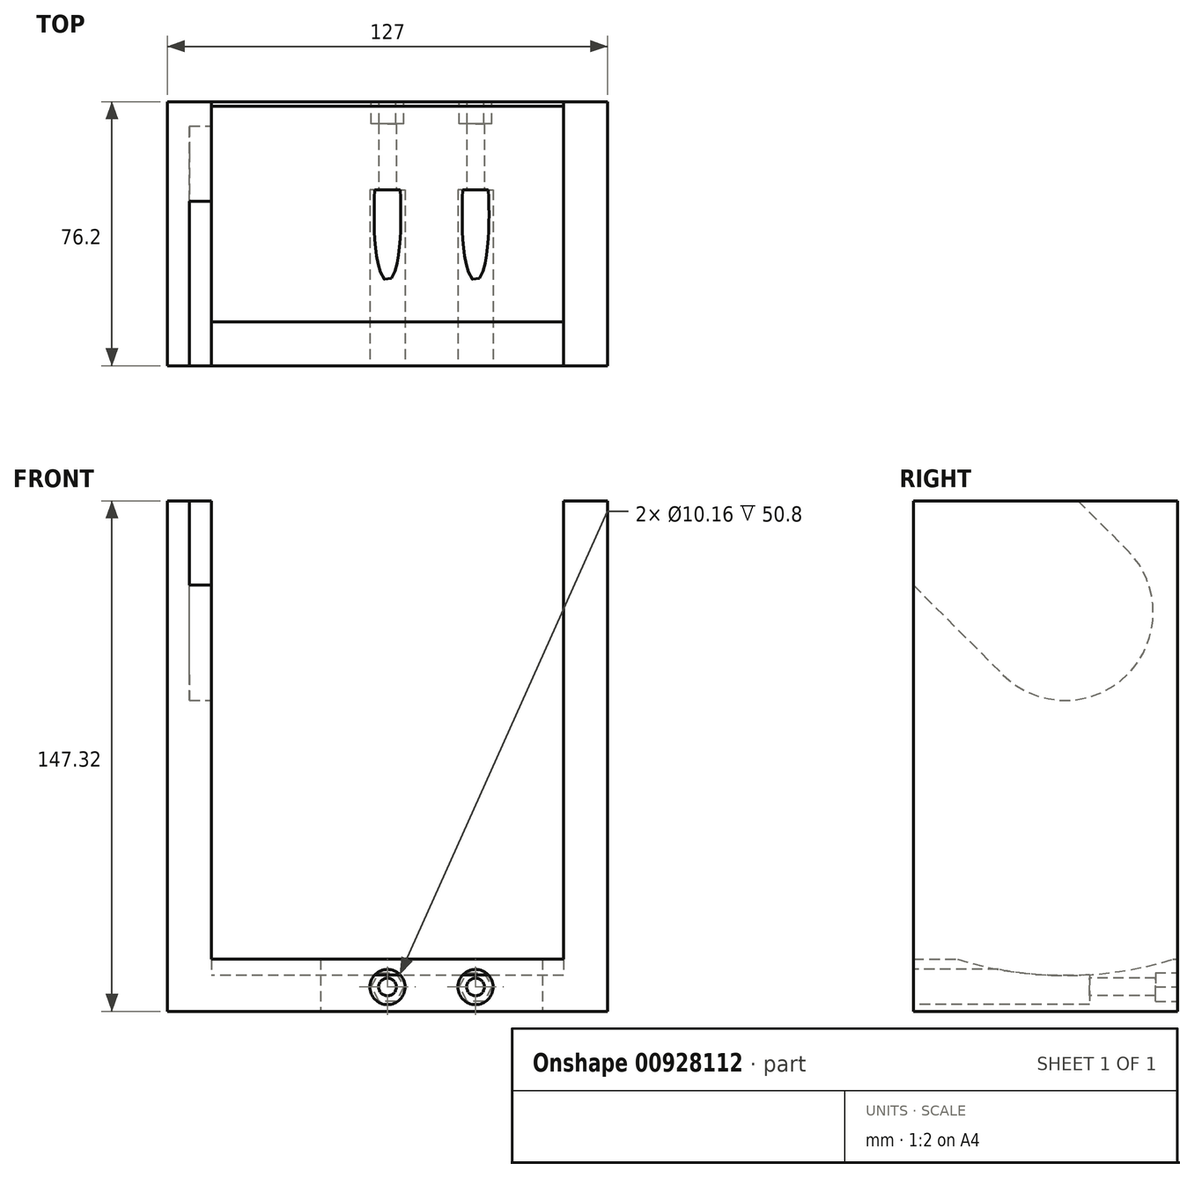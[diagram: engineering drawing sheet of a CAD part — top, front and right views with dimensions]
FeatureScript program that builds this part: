
annotation { "Feature Type Name" : "Feature", "Feature Type Description" : "" }
export const myFeature = defineFeature(function(context is Context, id is Id, definition is map)
    precondition{}
    {
        {
            var Q0;
            Q0=qCreatedBy(makeId("Top.planeOp"),FACE);
            var sketch = newSketch(context, id + "F0", { "sketchPlane" : qUnion([Q0])});
            skLineSegment(sketch, "E0.bottom", {"start": v(38.1, -38.1) * mm, "end": v(-38.1, -38.1) * mm});
            skLineSegment(sketch, "E0.top", {"start": v(38.1, 38.1) * mm, "end": v(-38.1, 38.1) * mm});
            skLineSegment(sketch, "E0.left", {"start": v(38.1, -38.1) * mm, "end": v(38.1, 38.1) * mm});
            skPoint(sketch, "E0.middle", {"position": v(0, 0) * mm});
            skLineSegment(sketch, "E1.bottom", {"start": v(-38.1, -38.1) * mm, "end": v(-63.5, -38.1) * mm});
            skLineSegment(sketch, "E1.top", {"start": v(-38.1, 38.1) * mm, "end": v(-63.5, 38.1) * mm});
            skLineSegment(sketch, "E1.right", {"start": v(-63.5, -38.1) * mm, "end": v(-63.5, 38.1) * mm});
            skSolve(sketch);
        }
        {
            var Q0;
            Q0 = qSketchRegion(id + "F0", true);
            extrude(context, id + "F1", {"entities" : qUnion([Q0]), "depth" : 15 * mm, "offsetDistance" : 25.4 * mm});
        }
        {
            var Q0;
            Q0=qCreatedBy(makeId("Top.planeOp"),FACE);
            var sketch = newSketch(context, id + "F2", { "sketchPlane" : qUnion([Q0])});
            skLineSegment(sketch, "E2.bottom", {"start": v(-63.5, -38.1) * mm, "end": v(-76.2, -38.1) * mm});
            skLineSegment(sketch, "E2.top", {"start": v(-63.5, 38.1) * mm, "end": v(-76.2, 38.1) * mm});
            skLineSegment(sketch, "E2.left", {"start": v(-63.5, -38.1) * mm, "end": v(-63.5, 38.1) * mm});
            skLineSegment(sketch, "E2.right", {"start": v(-76.2, -38.1) * mm, "end": v(-76.2, 38.1) * mm});
            skLineSegment(sketch, "E3.bottom", {"start": v(38.1, -38.1) * mm, "end": v(50.8, -38.1) * mm});
            skLineSegment(sketch, "E3.top", {"start": v(38.1, 38.1) * mm, "end": v(50.8, 38.1) * mm});
            skLineSegment(sketch, "E3.left", {"start": v(38.1, -38.1) * mm, "end": v(38.1, 38.1) * mm});
            skLineSegment(sketch, "E3.right", {"start": v(50.8, -38.1) * mm, "end": v(50.8, 38.1) * mm});
            skSolve(sketch);
        }
        {
            var Q0;
            Q0 = qSketchRegion(id + "F2", true);
            extrude(context, id + "F3", {"entities" : qUnion([Q0]), "operationType" : NewBodyOperationType.ADD, "depth" : 147.32 * mm, "offsetDistance" : 25.4 * mm});
        }
        {
            var Q0;
            Q0=makeQuery(id+"F3.boolean.opBoolean","MERGE",FACE,{"derivedFrom":[makeQuery(id+"F1.opExtrude","SWEPT_FACE",FACE,{"disambiguationData":[OSD([sQuery(id+"F0.wireOp",EDGE,"E0.bottom")])]}),makeQuery(id+"F3.opExtrude","SWEPT_FACE",FACE,{"disambiguationData":[OSD([sQuery(id+"F2.wireOp",EDGE,"E2.bottom")])]}),makeQuery(id+"F3.opExtrude","SWEPT_FACE",FACE,{"disambiguationData":[OSD([sQuery(id+"F2.wireOp",EDGE,"E3.bottom")])]})]});
            var sketch = newSketch(context, id + "F4", { "sketchPlane" : qUnion([Q0])});
            skCircle(sketch, "E4", {"center": v(-12.7, 7.01) * mm, "radius": 2.54 * mm});
            skCircle(sketch, "E5", {"center": v(12.7, 7.01) * mm, "radius": 2.54 * mm});
            skLineSegment(sketch, "E6", {"start": v(-12.7, 7.01) * mm, "end": v(12.7, 7.01) * mm, "construction": true});
            skLineSegment(sketch, "E7", {"start": v(0, 7.01) * mm, "end": v(0, 11.5) * mm});
            skSolve(sketch);
        }
        {
            var Q0;
            Q0 = qSketchRegion(id + "F4", true);
            extrude(context, id + "F5", {"entities" : qUnion([Q0]), "operationType" : NewBodyOperationType.REMOVE, "endBound" : BoundingType.THROUGH_ALL, "oppositeDirection" : true, "depth" : 25.4 * mm, "offsetDistance" : 25.4 * mm});
        }
        {
            var Q0;
            Q0=makeQuery(id+"F3.boolean.opBoolean","MERGE",FACE,{"derivedFrom":[makeQuery(id+"F1.opExtrude","SWEPT_FACE",FACE,{"disambiguationData":[OSD([sQuery(id+"F0.wireOp",EDGE,"E0.top")])]}),makeQuery(id+"F3.opExtrude","SWEPT_FACE",FACE,{"disambiguationData":[OSD([sQuery(id+"F2.wireOp",EDGE,"E2.top")])]}),makeQuery(id+"F3.opExtrude","SWEPT_FACE",FACE,{"disambiguationData":[OSD([sQuery(id+"F2.wireOp",EDGE,"E3.top")])]})]});
            var sketch = newSketch(context, id + "F6", { "sketchPlane" : qUnion([Q0])});
            skCircle(sketch, "E8.cCircle", {"center": v(-12.7, 7.01) * mm, "radius": 4.11 * mm, "construction": true});
            skLineSegment(sketch, "E8.0", {"start": v(-10.33, 11.12) * mm, "end": v(-7.95, 7.01) * mm});
            skLineSegment(sketch, "E8.1", {"start": v(-7.95, 7.01) * mm, "end": v(-10.33, 2.9) * mm});
            skLineSegment(sketch, "E8.2", {"start": v(-10.33, 2.9) * mm, "end": v(-15.07, 2.9) * mm});
            skLineSegment(sketch, "E8.3", {"start": v(-15.07, 2.9) * mm, "end": v(-17.45, 7.01) * mm});
            skLineSegment(sketch, "E8.4", {"start": v(-17.45, 7.01) * mm, "end": v(-15.07, 11.12) * mm});
            skLineSegment(sketch, "E8.5", {"start": v(-15.07, 11.12) * mm, "end": v(-10.33, 11.12) * mm});
            skPoint(sketch, "E8.0.midPoint", {"position": v(-9.14, 9.07) * mm});
            skCircle(sketch, "E9.cCircle", {"center": v(12.7, 7.01) * mm, "radius": 4.11 * mm, "construction": true});
            skLineSegment(sketch, "E9.0", {"start": v(15.07, 11.12) * mm, "end": v(17.45, 7.01) * mm});
            skLineSegment(sketch, "E9.1", {"start": v(17.45, 7.01) * mm, "end": v(15.07, 2.9) * mm});
            skLineSegment(sketch, "E9.2", {"start": v(15.07, 2.9) * mm, "end": v(10.33, 2.9) * mm});
            skLineSegment(sketch, "E9.3", {"start": v(10.33, 2.9) * mm, "end": v(7.95, 7.01) * mm});
            skLineSegment(sketch, "E9.4", {"start": v(7.95, 7.01) * mm, "end": v(10.33, 11.12) * mm});
            skLineSegment(sketch, "E9.5", {"start": v(10.33, 11.12) * mm, "end": v(15.07, 11.12) * mm});
            skPoint(sketch, "E9.0.midPoint", {"position": v(16.26, 9.07) * mm});
            skSolve(sketch);
        }
        {
            var Q0;
            Q0 = qSketchRegion(id + "F6", true);
            extrude(context, id + "F7", {"entities" : qUnion([Q0]), "operationType" : NewBodyOperationType.REMOVE, "oppositeDirection" : true, "depth" : 6.35 * mm, "offsetDistance" : 25.4 * mm});
        }
        {
            var Q0;
            Q0=makeQuery(id+"F3.boolean.opBoolean","MERGE",FACE,{"derivedFrom":[makeQuery(id+"F1.opExtrude","SWEPT_FACE",FACE,{"disambiguationData":[OSD([sQuery(id+"F0.wireOp",EDGE,"E0.bottom")])]}),makeQuery(id+"F3.opExtrude","SWEPT_FACE",FACE,{"disambiguationData":[OSD([sQuery(id+"F2.wireOp",EDGE,"E2.bottom")])]}),makeQuery(id+"F3.opExtrude","SWEPT_FACE",FACE,{"disambiguationData":[OSD([sQuery(id+"F2.wireOp",EDGE,"E3.bottom")])]})]});
            var sketch = newSketch(context, id + "F8", { "sketchPlane" : qUnion([Q0])});
            skCircle(sketch, "E10", {"center": v(-12.7, 7.01) * mm, "radius": 5.08 * mm});
            skCircle(sketch, "E11", {"center": v(12.7, 7.01) * mm, "radius": 5.08 * mm});
            skSolve(sketch);
        }
        {
            var Q0;
            Q0 = qSketchRegion(id + "F8", true);
            extrude(context, id + "F9", {"entities" : qUnion([Q0]), "operationType" : NewBodyOperationType.REMOVE, "oppositeDirection" : true, "depth" : 50.8 * mm, "offsetDistance" : 25.4 * mm});
        }
        {
            var Q0;
            Q0=makeQuery(id+"F3.opExtrude","SWEPT_FACE",FACE,{"disambiguationData":[OSD([sQuery(id+"F2.wireOp",EDGE,"E2.left")])]});
            var sketch = newSketch(context, id + "F10", { "sketchPlane" : qUnion([Q0])});
            skArc(sketch, "E12", {"start": v(-12.3, 97.16) * mm, "mid": v(23.62, 97.16) * mm, "end": v(23.62, 133.08) * mm});
            skLineSegment(sketch, "E13", {"start": v(-12.3, 97.16) * mm, "end": v(-38.1, 122.96) * mm});
            skLineSegment(sketch, "E14", {"start": v(23.62, 133.08) * mm, "end": v(9.38, 147.32) * mm});
            skLineSegment(sketch, "E15", {"start": v(9.38, 147.32) * mm, "end": v(-38.1, 147.32) * mm});
            skLineSegment(sketch, "E16", {"start": v(-38.1, 147.32) * mm, "end": v(-38.1, 122.96) * mm});
            skSolve(sketch);
        }
        {
            var Q0;
            Q0 = qSketchRegion(id + "F10", true);
            extrude(context, id + "F11", {"entities" : qUnion([Q0]), "operationType" : NewBodyOperationType.REMOVE, "oppositeDirection" : true, "depth" : 6.35 * mm, "offsetDistance" : 25.4 * mm, "hasSecondDirection" : true, "secondDirectionOppositeDirection" : false, "secondDirectionDepth" : 82.55 * mm});
        }
        {
            var Q0;
            Q0=makeQuery(id+"F1.opExtrude","CAP_FACE",FACE,{"disambiguationData":[OSD([sQuery(id+"F0.wireOp",EDGE,"E0.bottom"),sQuery(id+"F0.wireOp",EDGE,"E0.top"),sQuery(id+"F0.wireOp",EDGE,"E0.left"),sQuery(id+"F0.wireOp",EDGE,"E1.bottom"),sQuery(id+"F0.wireOp",EDGE,"E1.top"),sQuery(id+"F0.wireOp",EDGE,"E1.right")])],"isStart":false});
            var sketch = newSketch(context, id + "F12", { "sketchPlane" : qUnion([Q0])});
            skLineSegment(sketch, "E17", {"start": v(-12.7, 38.1) * mm, "end": v(-12.7, -38.1) * mm});
            skSolve(sketch);
        }
        {
            var Q0;
            Q0=qCreatedBy(makeId("Right.planeOp"),FACE);
            var Q1;
            Q1=sQuery(id+"F12.wireOp",EDGE,"E17");
            cPlane(context, id + "F13", {"entities" : qUnion([Q0, Q1]), "cplaneType" : CPlaneType.LINE_ANGLE, "offset" : 25.4 * mm, "angle" : 0 * degree, "width" : 152.4 * mm, "height" : 152.4 * mm});
        }
        {
            var Q0;
            Q0=qCreatedBy(id+"F13.planeOp",FACE);
            var sketch = newSketch(context, id + "F14", { "sketchPlane" : qUnion([Q0])});
            skArc(sketch, "E18", {"start": v(-36.73, 15.01) * mm, "mid": v(-5.66, 10.3) * mm, "end": v(25.4, 15.01) * mm});
            skLineSegment(sketch, "E19", {"start": v(-36.73, 15.01) * mm, "end": v(25.4, 15.01) * mm});
            skSolve(sketch);
        }
        {
            var Q0;
            Q0 = qSketchRegion(id + "F14", true);
            extrude(context, id + "F15", {"entities" : qUnion([Q0]), "operationType" : NewBodyOperationType.REMOVE, "endBound" : BoundingType.SYMMETRIC, "oppositeDirection" : true, "depth" : 101.6 * mm, "offsetDistance" : 25.4 * mm});
        }
        {
            var Q0;
            Q0=makeQuery(id+"F3.boolean.opBoolean","MERGE",FACE,{"derivedFrom":[makeQuery(id+"F1.opExtrude","SWEPT_FACE",FACE,{"disambiguationData":[OSD([sQuery(id+"F0.wireOp",EDGE,"E0.top"),sQuery(id+"F0.wireOp",EDGE,"E1.top")])]}),makeQuery(id+"F3.opExtrude","SWEPT_FACE",FACE,{"disambiguationData":[OSD([sQuery(id+"F2.wireOp",EDGE,"E2.top")])]}),makeQuery(id+"F3.opExtrude","SWEPT_FACE",FACE,{"disambiguationData":[OSD([sQuery(id+"F2.wireOp",EDGE,"E3.top")])]})]});
            var sketch = newSketch(context, id + "F16", { "sketchPlane" : qUnion([Q0])});
            skLineSegment(sketch, "E20.bottom", {"start": v(-31.95, 15.01) * mm, "end": v(31.95, 15.01) * mm});
            skLineSegment(sketch, "E20.top", {"start": v(-31.95, 0) * mm, "end": v(31.95, 0) * mm});
            skLineSegment(sketch, "E20.left", {"start": v(-31.95, 15.01) * mm, "end": v(-31.95, 0) * mm});
            skLineSegment(sketch, "E20.right", {"start": v(31.95, 15.01) * mm, "end": v(31.95, 0) * mm});
            skLineSegment(sketch, "E21", {"start": v(-31.95, 7.5) * mm, "end": v(0, 7.5) * mm, "construction": true});
            skLineSegment(sketch, "E22", {"start": v(0, 7.5) * mm, "end": v(31.95, 7.5) * mm, "construction": true});
            skSolve(sketch);
        }
        {
            var Q0;
            Q0 = qSketchRegion(id + "F16", true);
            extrude(context, id + "F17", {"entities" : qUnion([Q0]), "operationType" : NewBodyOperationType.REMOVE, "oppositeDirection" : true, "depth" : 0.1 * mm, "offsetDistance" : 25.4 * mm});
        }
    });
